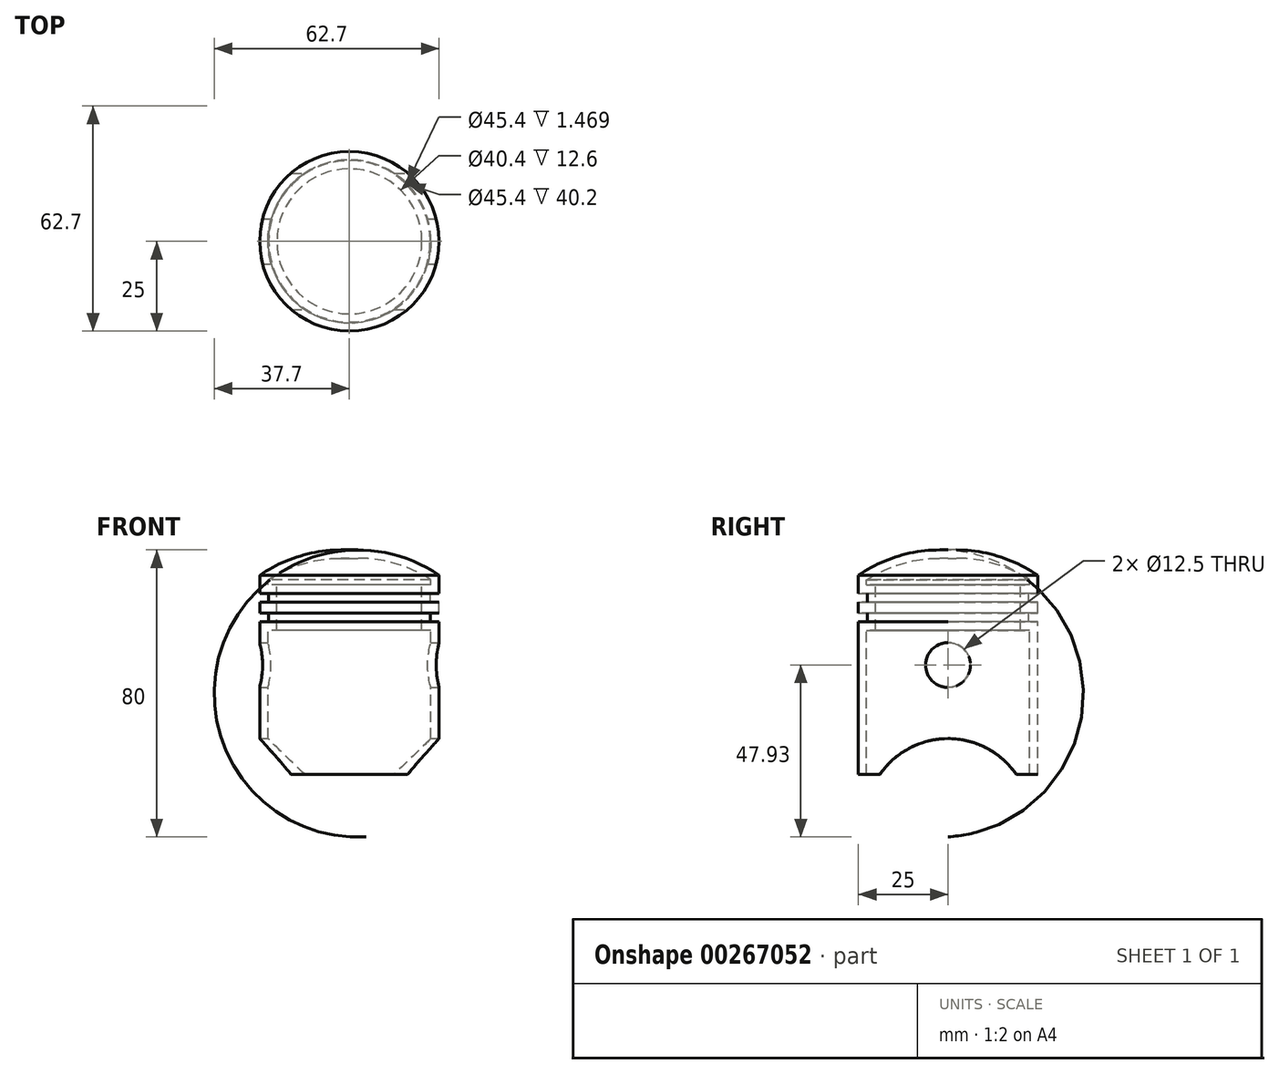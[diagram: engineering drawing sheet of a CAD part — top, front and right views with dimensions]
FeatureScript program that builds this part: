
annotation { "Feature Type Name" : "Feature", "Feature Type Description" : "" }
export const myFeature = defineFeature(function(context is Context, id is Id, definition is map)
    precondition{}
    {
        {
            var Q0;
            Q0=qCreatedBy(makeId("Front.planeOp"),FACE);
            var sketch = newSketch(context, id + "F0", { "sketchPlane" : qUnion([Q0])});
            skLineSegment(sketch, "E0", {"start": v(25, 0) * mm, "end": v(25, 42.5) * mm});
            skLineSegment(sketch, "E1", {"start": v(25, 42.5) * mm, "end": v(22.5, 42.5) * mm});
            skLineSegment(sketch, "E2", {"start": v(22.5, 42.5) * mm, "end": v(22.5, 45) * mm});
            skLineSegment(sketch, "E3", {"start": v(22.5, 45) * mm, "end": v(25, 45) * mm});
            skLineSegment(sketch, "E4", {"start": v(25, 45) * mm, "end": v(25, 48) * mm});
            skLineSegment(sketch, "E5", {"start": v(25, 48) * mm, "end": v(22.5, 48) * mm});
            skLineSegment(sketch, "E6", {"start": v(22.5, 48) * mm, "end": v(22.5, 50.5) * mm});
            skLineSegment(sketch, "E7", {"start": v(22.5, 50.5) * mm, "end": v(25, 50.5) * mm});
            skLineSegment(sketch, "E8", {"start": v(25, 50.5) * mm, "end": v(25, 55.5) * mm});
            skArc(sketch, "E9", {"start": v(25, 55.5) * mm, "mid": v(13.08, 61.08) * mm, "end": v(0, 62.5) * mm});
            skLineSegment(sketch, "E10", {"start": v(0, 62.5) * mm, "end": v(0, 0) * mm, "construction": true});
            skLineSegment(sketch, "E11", {"start": v(25, 0) * mm, "end": v(0, 0) * mm, "construction": true});
            skLineSegment(sketch, "E12.0", {"start": v(20.2, 52.8) * mm, "end": v(22.7, 52.8) * mm});
            skLineSegment(sketch, "E12.1", {"start": v(20.2, 47.3) * mm, "end": v(20.2, 52.8) * mm});
            skLineSegment(sketch, "E12.2", {"start": v(22.7, 52.8) * mm, "end": v(22.7, 54.27) * mm});
            skLineSegment(sketch, "E12.3", {"start": v(20.2, 40.2) * mm, "end": v(20.2, 47.3) * mm});
            skLineSegment(sketch, "E12.4", {"start": v(22.7, 40.2) * mm, "end": v(20.2, 40.2) * mm});
            skArc(sketch, "E12.5", {"start": v(22.7, 54.27) * mm, "mid": v(12.93, 58.74) * mm, "end": v(2.3, 60.27) * mm});
            skLineSegment(sketch, "E12.6", {"start": v(2.3, 60.27) * mm, "end": v(2.3, 2.3) * mm, "construction": true});
            skLineSegment(sketch, "E12.7", {"start": v(22.7, 2.3) * mm, "end": v(2.3, 2.3) * mm, "construction": true});
            skLineSegment(sketch, "E12.8", {"start": v(22.7, 2.3) * mm, "end": v(22.7, 40.2) * mm});
            skLineSegment(sketch, "E13", {"start": v(2.3, 60.27) * mm, "end": v(0, 60.27) * mm});
            skLineSegment(sketch, "E14", {"start": v(22.7, 2.3) * mm, "end": v(22.7, 0) * mm});
            skLineSegment(sketch, "E15", {"start": v(0, 62.5) * mm, "end": v(0, 60.27) * mm});
            skLineSegment(sketch, "E16", {"start": v(25, 0) * mm, "end": v(22.7, 0) * mm});
            skSolve(sketch);
        }
        {
            var Q0;
            Q0 = qSketchRegion(id + "F0", true);
            var Q1;
            Q1=sQuery(id+"F0.wireOp",EDGE,"E10");
            revolve(context, id + "F1", {"entities" : qUnion([Q0]), "axis" : qUnion([Q1]), "revolveType" : RevolveType.FULL});
        }
        {
            var Q0;
            Q0=qCreatedBy(makeId("Right.planeOp"),FACE);
            var sketch = newSketch(context, id + "F2", { "sketchPlane" : qUnion([Q0])});
            skLineSegment(sketch, "E17", {"start": v(-25, 0) * mm, "end": v(-25, 42.5) * mm});
            skLineSegment(sketch, "E18", {"start": v(25, 42.5) * mm, "end": v(25, 0) * mm});
            skLineSegment(sketch, "E19.0", {"start": v(-25, 0) * mm, "end": v(25, 0) * mm});
            skArc(sketch, "E20", {"start": v(19, 0) * mm, "mid": v(0, 10) * mm, "end": v(-19, 0) * mm});
            skSolve(sketch);
        }
        {
            var Q0;
            Q0 = qSketchRegion(id + "F2", true);
            extrude(context, id + "F3", {"entities" : qUnion([Q0]), "operationType" : NewBodyOperationType.REMOVE, "endBound" : BoundingType.SYMMETRIC, "oppositeDirection" : true, "depth" : 58.8 * mm});
        }
        {
            var Q0;
            Q0=qCreatedBy(makeId("Right.planeOp"),FACE);
            var sketch = newSketch(context, id + "F4", { "sketchPlane" : qUnion([Q0])});
            skCircle(sketch, "E21", {"center": v(0, 30.5) * mm, "radius": 6.25 * mm});
            skSolve(sketch);
        }
        {
            var Q0;
            Q0 = qSketchRegion(id + "F4", true);
            extrude(context, id + "F5", {"entities" : qUnion([Q0]), "operationType" : NewBodyOperationType.REMOVE, "endBound" : BoundingType.SYMMETRIC, "oppositeDirection" : true, "depth" : 82.6 * mm});
        }
    });
